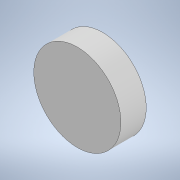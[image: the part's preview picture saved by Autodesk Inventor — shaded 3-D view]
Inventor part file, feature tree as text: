
AUTODESK INVENTOR PART (.ipt)
format: ipt  version: 2021 (Build 250183000, 183)  size: 99,840 bytes
history: native  units: mm
features: other x1, extrude x1, sketch x1
ambient origin geometry x8: Origin, YZ Plane, XZ Plane, XY Plane, X Axis, Y Axis, Z Axis, Center Point
bodies: Body1 (feature_tree)
feature tree (3):
  other  "Твердое тело1"
  extrude  "Выдавливание1"  Depth=55.0mm
  sketch  "Эскиз1"
